FCSTD DOCUMENT  (FreeCAD 0.19R)
Label: alphacool-xt45-200
License: All rights reserved
LicenseURL: http://en.wikipedia.org/wiki/All_rights_reserved
objects: PartDesign::CoordinateSystem×2, Part::Feature×1, PartDesign::FeatureBase×1, PartDesign::Body×1, App::Part×1
note: 5 computed .brp shape members not serialized (recipe doc carries the construction recipe); baked Part::Feature solids carry a one-line shape summary decoded from their .brp

FEATURE [Part::Feature] Solid  label="10107-000-Alphacool NexXxoS XT45 Full Copper 200_Shrinkwrap_1"
  shape: bbox 200 x 47 x 239.2 mm, 6627 faces (baked)
FEATURE [PartDesign::CoordinateSystem] LCS_1  label="top-fan-mount"
  AttacherType = Attacher::AttachEngine3D
  AttachmentOffset = pos=(0,0,0) rot=(0,0,-1;1.5708rad)
  MapMode = 11
  Placement = pos=(-122.361,20.0881,-172.936) rot=(-1,0,0;1.5708rad)
  Support = -> [Solid]
FEATURE [PartDesign::FeatureBase] BaseFeature
  BaseFeature = -> Solid
FEATURE [PartDesign::Body] Body
  BaseFeature = -> Solid
  Group = -> [BaseFeature]
  Origin = -> Origin001
  Tip = -> BaseFeature
FEATURE [PartDesign::CoordinateSystem] bottom_fan_mount
  AttacherType = Attacher::AttachEngine3D
  AttachmentOffset = pos=(0,0,-46.5) rot=(0,0,-1;1.5708rad)
  MapMode = 11
  Placement = pos=(-122.361,-26.4119,-172.936) rot=(-1,0,0;1.5708rad)
  Support = -> [BaseFeature]
FEATURE [App::Part] Part
  Group = -> [Body,bottom_fan_mount]
  Origin = -> Origin
